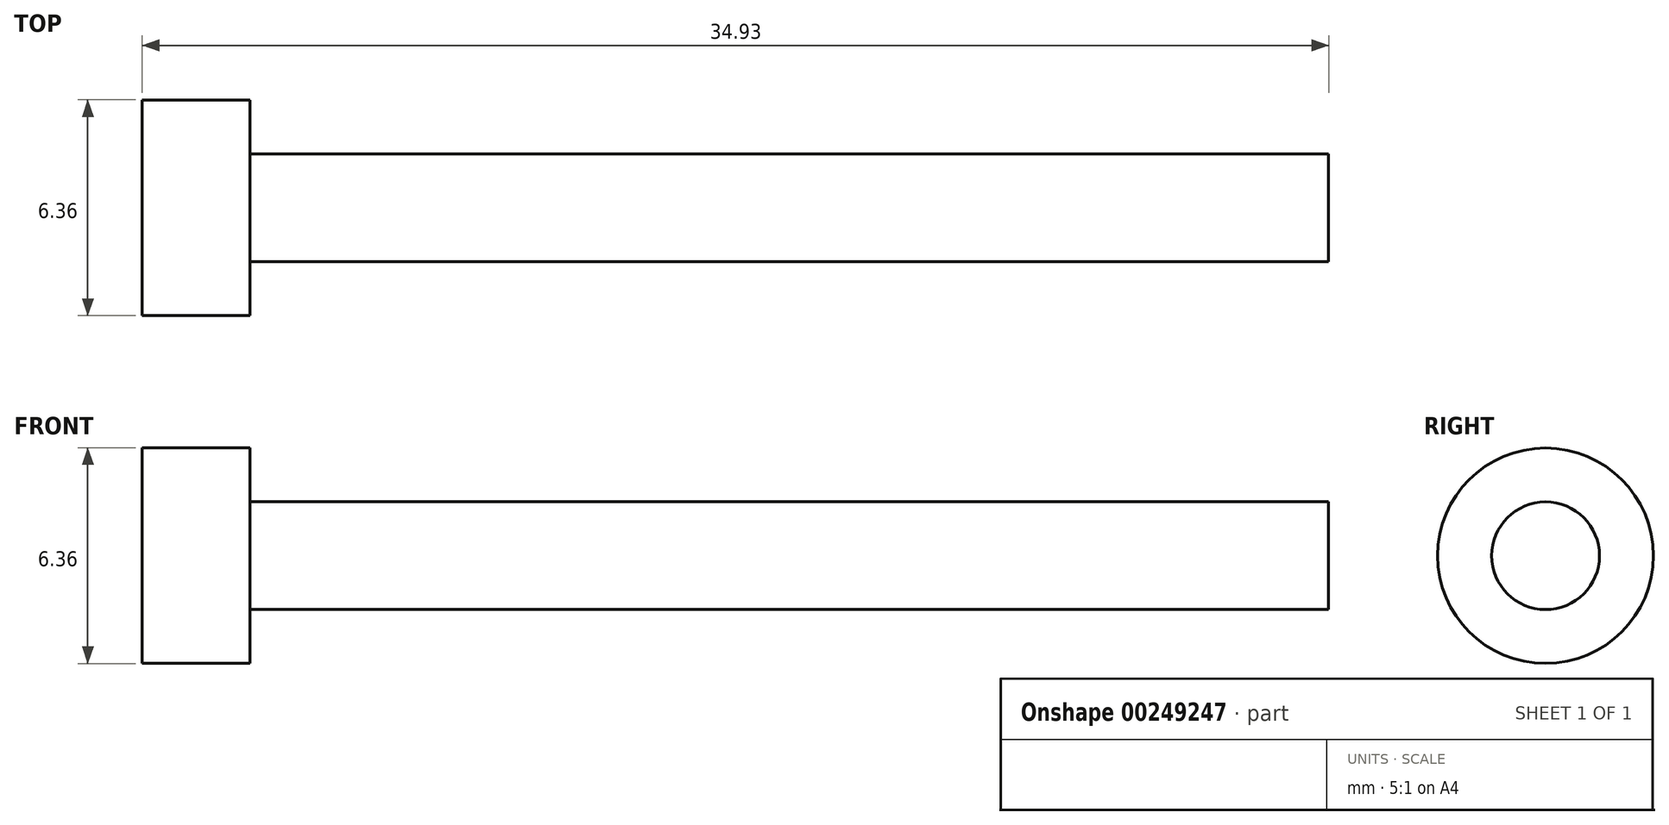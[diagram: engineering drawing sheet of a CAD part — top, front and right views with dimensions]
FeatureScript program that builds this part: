
annotation { "Feature Type Name" : "Feature", "Feature Type Description" : "" }
export const myFeature = defineFeature(function(context is Context, id is Id, definition is map)
    precondition{}
    {
        {
            var Q0;
            Q0=qCreatedBy(makeId("Right.planeOp"),FACE);
            var sketch = newSketch(context, id + "F0", { "sketchPlane" : qUnion([Q0])});
            skCircle(sketch, "E0", {"center": v(0, 0) * mm, "radius": 3.18 * mm});
            skSolve(sketch);
        }
        {
            var Q0;
            Q0=makeQuery(id+"F0.imprint","IMPRINT",FACE,{"disambiguationData":[TD([[makeQuery(id+"F0.imprint","IMPRINT",EDGE,{"derivedFrom":sQuery(id+"F0.wireOp",EDGE,"E0")}),1.0]])]});
            var Q1;
            Q1=sQuery(id+"F0.wireOp",EDGE,"E0");
            extrude(context, id + "F1", {"entities" : qUnion([Q0]), "surfaceEntities" : qUnion([Q1]), "depth" : 3.17 * mm});
        }
        {
            var Q0;
            Q0=makeQuery(id+"F1.opExtrude","CAP_FACE",FACE,{"disambiguationData":[OSD([sQuery(id+"F0.wireOp",EDGE,"E0")])],"isStart":false});
            var sketch = newSketch(context, id + "F2", { "sketchPlane" : qUnion([Q0])});
            skCircle(sketch, "E1", {"center": v(0, 0) * mm, "radius": 1.59 * mm});
            skSolve(sketch);
        }
        {
            var Q0;
            Q0=makeQuery(id+"F2.imprint","IMPRINT",FACE,{"disambiguationData":[TD([[makeQuery(id+"F2.imprint","IMPRINT",EDGE,{"derivedFrom":sQuery(id+"F2.wireOp",EDGE,"E1")}),1.0]])]});
            var Q1;
            Q1=sQuery(id+"F2.wireOp",EDGE,"E1");
            extrude(context, id + "F3", {"entities" : qUnion([Q0]), "operationType" : NewBodyOperationType.ADD, "surfaceEntities" : qUnion([Q1]), "depth" : 31.75 * mm});
        }
    });
